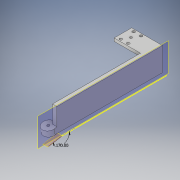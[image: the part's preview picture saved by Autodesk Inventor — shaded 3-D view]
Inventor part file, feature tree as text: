
AUTODESK INVENTOR PART (.ipt)
format: ipt  version: 2017 (Build 210142000, 142)  size: 200,704 bytes
history: native  units: in
note: dims shown in document units (in); Inventor stores cm internally (conversion verified against a paired STEP export)
features: sketch x8, projected_geometry x7, extrude x4, hole x3, plane x2, mirror x1
ambient origin geometry x8: Origin, YZ Plane, XZ Plane, XY Plane, X Axis, Y Axis, Z Axis, Center Point
bodies: Solid2 (feature_tree)
feature tree (25):
  extrude  "Extrusion2"  Depth=4.5in
  sketch  "Sketch3"  dims[d8=0.1875in d9=0.0in d10=1.1681in]
  plane  "Work Plane1"
  sketch  "Sketch4"  dims[d18=0.125in d19=0.0in d28=0.5in]
  extrude  "Extrusion4"  Depth=0.1875in
  extrude  "Extrusion6"  Depth=0.125in
  extrude  "Extrusion9"  Depth=0.1875in
  hole  "Hole1"  [1 undecoded]
  hole  "Hole2"  [1 undecoded]
  hole  "Hole3"  [1 undecoded]
  plane  "Work Plane2"
  mirror  "Mirror1"
  sketch  "Sketch2"  dims[d6=1.0in d7=4.5in]
  projected_geometry  "Projected Loop1"
  sketch  "Sketch5"  dims[d29=0.1875in d30=0.0625in]
  projected_geometry  "Projected Loop2"
  sketch  "Sketch10"  dims[d32=0.25in d33=0.0in d40=0.075in]
  projected_geometry  "Projected Loop8"
  projected_geometry  "Projected Loop9"
  sketch  "Sketch11"  dims[d41=0.4846in d42=0.2423in]
  projected_geometry  "Projected Loop10"
  sketch  "Sketch12"  dims[d43=0.6871in d44=0.35in]
  projected_geometry  "Projected Loop11"
  sketch  "Sketch13"  dims[d45=0.1in d46=0.0in d47=1.3125in d48=0.1875in d49=0.75in d50=0.6299in d53=0.75in d54=1.125in d55=0.375in d56=0.315in d57=0.1575in d58=0.625in d59=0.115in d60=0.75in d61=0.375in d62=0.25in d63=0.5635in d64=1.0in d65=0.8108in d66=0.1in d67=0.75in d68=0.375in d69=0.25in d70=0.5635in d71=1.0in d72=0.8108in d73=0.1in d74=0.75in d75=0.375in d76=0.25in d77=0.5635in d78=1.0in d79=0.8108in]
  projected_geometry  "Projected Loop12"
note: 3 required parameter values undecoded (feature->parameter linkage not recoverable at this tier; creation-order binding heuristic only, values carry confidence <= 0.55)
